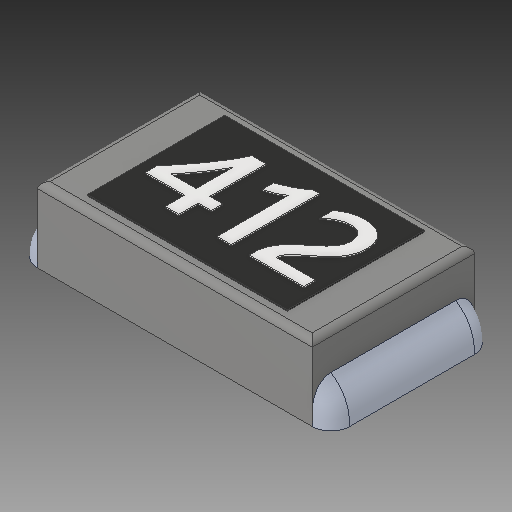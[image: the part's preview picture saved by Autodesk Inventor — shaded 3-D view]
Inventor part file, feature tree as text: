
AUTODESK INVENTOR PART (.ipt)
format: ipt  version: 2018.3 (Build 223284000, 284)  size: 225,792 bytes
history: native  units: mm
features: other x4, fillet x1, mirror x1
ambient origin geometry x8: Origin, YZ Plane, XZ Plane, XY Plane, X Axis, Y Axis, Z Axis, Center Point
bodies: Body1 (feature_tree), Body2 (feature_tree), Body3 (feature_tree)
feature tree (6):
  other  "Sólido1"
  other  "Sólido2"
  other  "Sólido3"
  fillet  "Fillet2"  [1 undecoded]
  mirror  "Mirror1"
  other  "Boss-Extrude4"
note: 1 required parameter value undecoded (feature->parameter linkage not recoverable at this tier; creation-order binding heuristic only, values carry confidence <= 0.55)
